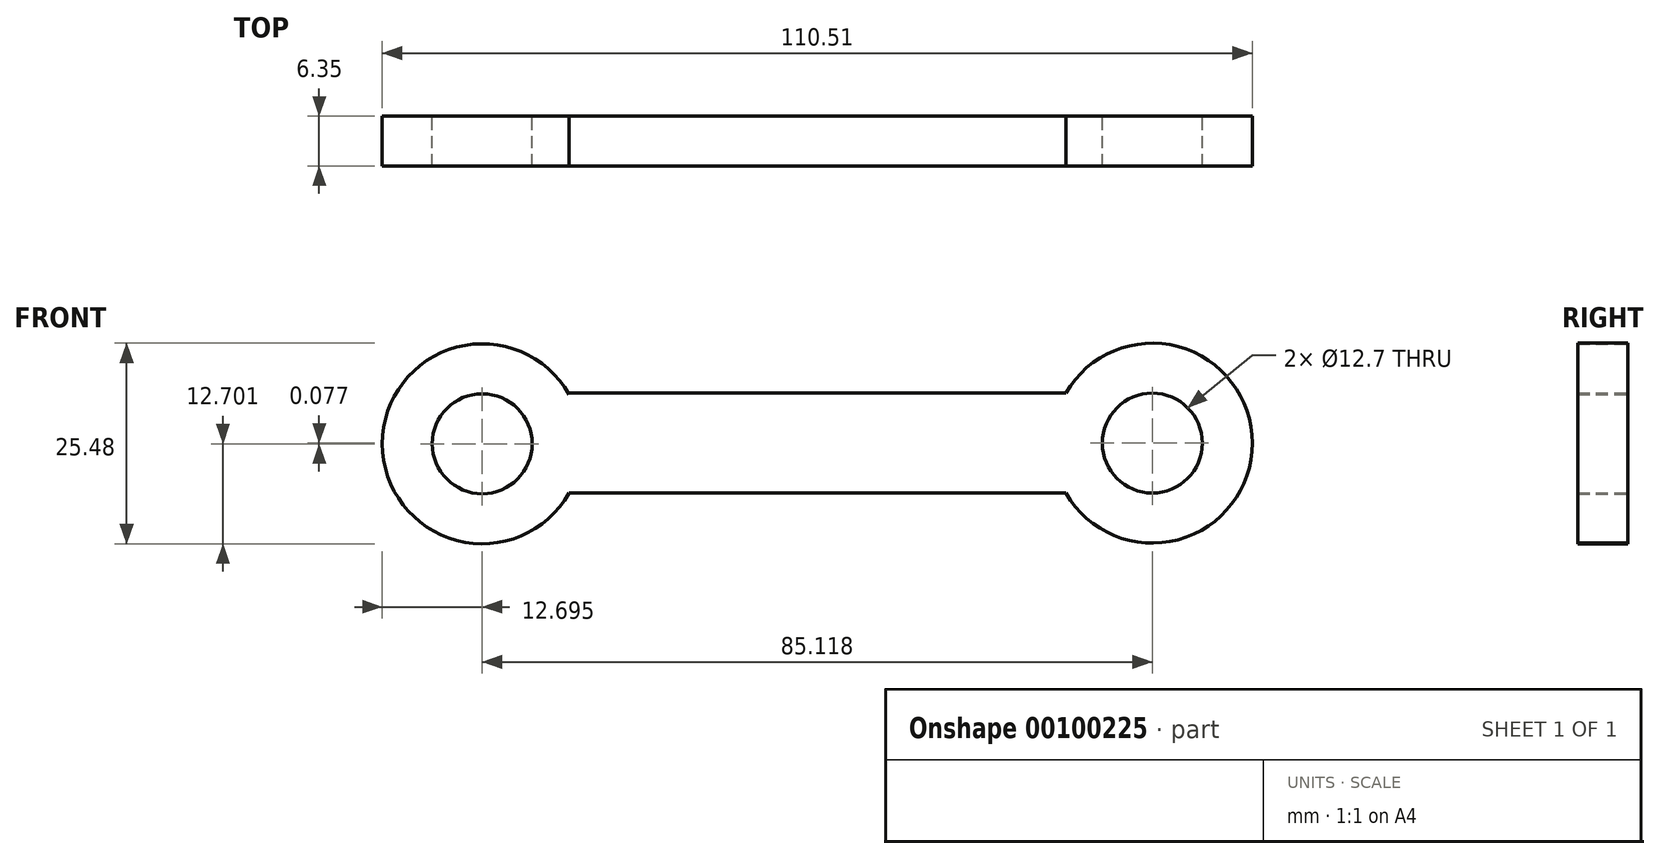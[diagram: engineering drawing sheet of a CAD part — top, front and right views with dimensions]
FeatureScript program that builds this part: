
annotation { "Feature Type Name" : "Feature", "Feature Type Description" : "" }
export const myFeature = defineFeature(function(context is Context, id is Id, definition is map)
    precondition{}
    {
        {
            var Q0;
            Q0=qCreatedBy(makeId("Front.planeOp"),FACE);
            var sketch = newSketch(context, id + "F0", { "sketchPlane" : qUnion([Q0])});
            skLineSegment(sketch, "E0", {"start": v(-39.42, 21.8) * mm, "end": v(23.65, 21.8) * mm});
            skLineSegment(sketch, "E1", {"start": v(23.65, 9.1) * mm, "end": v(-39.42, 9.1) * mm});
            skCircle(sketch, "E2", {"center": v(-50.46, 15.37) * mm, "radius": 12.7 * mm});
            skCircle(sketch, "E3", {"center": v(34.65, 15.45) * mm, "radius": 12.7 * mm});
            skPoint(sketch, "E4", {"position": v(-39.42, 21.8) * mm});
            skPoint(sketch, "E5", {"position": v(-39.42, 9.1) * mm});
            skPoint(sketch, "E6", {"position": v(23.65, 21.8) * mm});
            skPoint(sketch, "E7", {"position": v(23.65, 9.1) * mm});
            skCircle(sketch, "E8", {"center": v(-50.46, 15.37) * mm, "radius": 6.35 * mm});
            skCircle(sketch, "E9", {"center": v(34.65, 15.45) * mm, "radius": 6.35 * mm});
            skLineSegment(sketch, "E10", {"start": v(-39.42, 21.8) * mm, "end": v(-39.42, 9.1) * mm});
            skSolve(sketch);
        }
        {
            var Q0;
            {var subQ1=sQuery(id+"F0.wireOp",EDGE,"E0");Q0=makeQuery(id+"F0.imprint","IMPRINT",FACE,{"disambiguationData":[TD([[makeQuery(id+"F0.imprint","IMPRINT",EDGE,{"derivedFrom":subQ1}),-1.0]])]});}
            var Q1;
            Q1=makeQuery(id+"F0.imprint","IMPRINT",FACE,{"disambiguationData":[TD([[makeQuery(id+"F0.imprint","IMPRINT",EDGE,{"derivedFrom":sQuery(id+"F0.wireOp",EDGE,"E8")}),-1.0]])]});
            var Q2;
            {var subQ0=sQuery(id+"F0.wireOp",EDGE,"E10");var subQ1=sQuery(id+"F0.wireOp",EDGE,"E2");var subQ3=makeQuery(id+"F0.imprint","INTERSECT",VERTEX,{"derivedFrom":[subQ1,subQ0]});Q2=makeQuery(id+"F0.imprint","IMPRINT",FACE,{"disambiguationData":[TD([[makeQuery(id+"F0.imprint","IMPRINT",EDGE,{"disambiguationData":[TD([[subQ3,1.0]])],"derivedFrom":subQ1}),1.0]])]});}
            var Q3;
            Q3=makeQuery(id+"F0.imprint","IMPRINT",FACE,{"disambiguationData":[TD([[makeQuery(id+"F0.imprint","IMPRINT",EDGE,{"derivedFrom":sQuery(id+"F0.wireOp",EDGE,"E9")}),-1.0]])]});
            extrude(context, id + "F1", {"entities" : qUnion([Q0, Q1, Q2, Q3]), "depth" : 6.35 * mm});
        }
    });
